# Revit family: QF_ELECTROLUXPROFESSIONAL_1LSNSS_TD6-30_S
name_source: partatom
category: Attrezzature speciali
units: mm (PartAtom-declared; Revit-internal decimal feet)

## family parameters
Basato su piano di lavoro = No
Condiviso = No
Punto di calcolo locali = No
Quota connettore circolare = Usa diametro
Sempre verticale = Sì
Taglio con vuoti quando caricato = No
Tipo di parte = Normale

## types (12) — shared parameters
Depth Actual = 1445 mm
Height Actual = 1855 mm  [stored 6.08596 ft]
Latent Heat Output = 0.0
Length Actual = 960 mm  [stored 3.14961 ft]
Modello = TD6-30
Produttore = Electrolux Professional
Sensible Heat Output = 0.0
Steam Pounds per Hour = 65
URL = www.electroluxprofessional.com
Weight = 304
zero-valued in all types: Gas KW, Prospetto di default

## per-type parameters (varying)
| type | Cycle | Descrizione | Item Number | Phase | Volts | Watts |
| 9872330161 | 50 Hz | TUMBLE DRYER TD6-30 30KG GALVA.DRUM STEAM 36KW 380-415/50/3N COMPASS PRO 6G82 SLVR/SLVR DO.RIGHT REV DISCON DMPR | 1LT69H | 3 | 415 V | 1500 W |
| 9872330073 | 60 Hz | TUMBLE DRYER TD6-30 MARINE 30KG SST DRUM STEAM 36KW 208-240/60/1 COMPASS PRO 6G81 SLVR/SLVR DO.RIGHT REV MB STOP DIS... | 1L0GE1 | 1 | 240 V | 1700 W |
| 9872330127 | 60 Hz | TUMBLE DRYER TD6-30 30KG SST DRUM STEAM 36KW 208-240/60/1 COMPASS PRO 6G81 SLVR/SLVR DO.RIGHT REV MB STOP DISCON DMPR | 1L0H38 | 1 | 240 V | 1700 W |
| 9872330030 | 50 Hz | TUMBLE DRYER TD6-30 30KG GALVA.DRUM STEAM 36KW 380-415/50/3 COMPASS PRO 6G81 SLVR/SLVR DO.RIGHT REV MB STOP DISCON DMPR | 1L0G5J | 3 | 415 V | 1500 W |
| 9872330134 | 60 Hz | TUMBLE DRYER TD6-30 MARINE 30KG SST DRUM STEAM 36KW 200/60/3 COMPASS PRO 6G86 SST/SLVR DO.RIGHT REV DISCON DMPR | 1LT5Z9 | 3 | 200 V | 1500 W |
| 9872330142 | 50 Hz | TUMBLE DRYER TD6-30 MARINE 30KG SST DRUM STEAM 36KW 200/50/3 COMPASS PRO 6G86 SST/SLVR DO.RIGHT REV DISCON DMPR | 1L0H7X | 3 | 200 V | 1500 W |
| 9872330095 | 50 Hz | TUMBLE DRYER TD6-30 30KG SST DRUM STEAM 36KW 380-415/50/3 COMPASS PRO 6G82 SLVR/SLVR DO.RIGHT REV STOP DISCON DMPR | 1LSPEX | 3 | 415 V | 1500 W |
| 9872330100 | 60 Hz | TUMBLE DRYER TD6-30 30KG GALVA.DRUM STEAM 36KW 220/60/1 COMPASS PRO 6G82 SLVR/SLVR DO.LEFT REV DISCON DMPR | 1L0GW9 | 1 | 220 V | 1700 W |
| 9872330018 | 50 Hz | TUMBLE DRYER TD6-30 30KG SST DRUM STEAM 36KW 380-415/50/3N COMPASS PRO 6G81 SLVR/SLVR DO.RIGHT REV MB STOP DISCON DMPR | 1L0G56 | 3 | 415 V | 1500 W |
| 9872330025 | 50 Hz | TUMBLE DRYER TD6-30 30KG GALVA.DRUM STEAM 36KW 380-415/50/3N COMPASS PRO 6G82 SLVR/SLVR DO.RIGHT REV DISCON DMPR | 1L0G5D | 3 | 415 V | 1500 W |
| 9872330026 | 50 Hz | TUMBLE DRYER TD6-30 30KG SST DRUM STEAM 36KW 380-415/50/3N COMPASS PRO 6G82 SLVR/SLVR DO.RIGHT REV DISCON DMPR | 1L0G5E | 3 | 415 V | 1500 W |
| 9872330068 | 50 Hz | TUMBLE DRYER TD6-30 30KG SST DRUM STEAM 36KW 380-415/50/3N COMPASS PRO 6G81 SST/SST DO.LEFT REV MB STOP DISCON DMPR | 1LA1DB | 3 | 415 V | 1500 W |

note: [stored X ft] marks values corroborated as IEEE doubles in the binary element streams (Revit-internal decimal feet)

## geometry (parser evidence)
native form markers: Blend x8
no freeform markers — native parametric forms only
